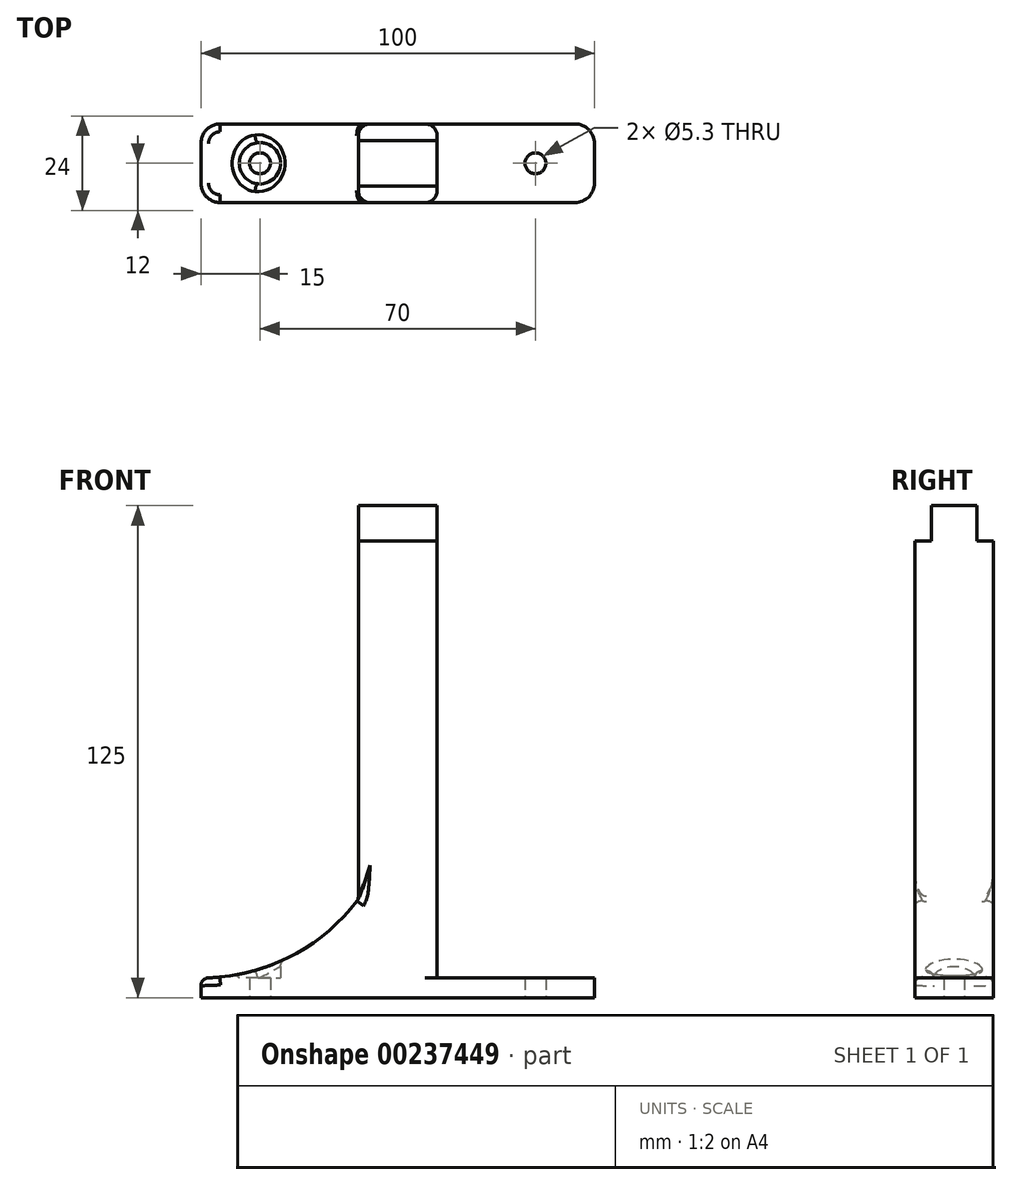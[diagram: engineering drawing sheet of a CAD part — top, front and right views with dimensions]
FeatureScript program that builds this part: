
annotation { "Feature Type Name" : "Feature", "Feature Type Description" : "" }
export const myFeature = defineFeature(function(context is Context, id is Id, definition is map)
    precondition{}
    {
        {
            var Q0;
            Q0=qCreatedBy(makeId("Front.planeOp"),FACE);
            var sketch = newSketch(context, id + "F0", { "sketchPlane" : qUnion([Q0])});
            skLineSegment(sketch, "E0.bottom", {"start": v(0, 0) * mm, "end": v(20, 0) * mm});
            skLineSegment(sketch, "E0.top", {"start": v(0, 120) * mm, "end": v(20, 120) * mm});
            skLineSegment(sketch, "E0.left", {"start": v(0, 0) * mm, "end": v(0, 120) * mm});
            skLineSegment(sketch, "E0.right", {"start": v(20, 0) * mm, "end": v(20, 120) * mm});
            skLineSegment(sketch, "E1", {"start": v(0, 20) * mm, "end": v(20, 20) * mm});
            skPoint(sketch, "E2.firstSnap0", {"position": v(10, 0) * mm});
            skLineSegment(sketch, "E2.bottom", {"start": v(60, 0) * mm, "end": v(-40, 0) * mm});
            skLineSegment(sketch, "E2.top", {"start": v(60, -5) * mm, "end": v(-40, -5) * mm});
            skLineSegment(sketch, "E2.left", {"start": v(60, 0) * mm, "end": v(60, -5) * mm});
            skLineSegment(sketch, "E2.right", {"start": v(-40, 0) * mm, "end": v(-40, -5) * mm});
            skLineSegment(sketch, "E3", {"start": v(10, 0) * mm, "end": v(10, 120) * mm, "construction": true});
            skArc(sketch, "E4", {"start": v(-40, 0) * mm, "mid": v(-17.64, 5.28) * mm, "end": v(0, 20) * mm});
            skArc(sketch, "E5.MirrorCS", {"start": v(60, 0) * mm, "mid": v(37.64, 5.28) * mm, "end": v(20, 20) * mm});
            skSolve(sketch);
        }
        {
            var Q0;
            {var subQ0=sQuery(id+"F0.wireOp",EDGE,"E0.top");Q0=makeQuery(id+"F0.imprint","IMPRINT",FACE,{"disambiguationData":[TD([[makeQuery(id+"F0.imprint","IMPRINT",EDGE,{"derivedFrom":subQ0}),-1.0]])]});}
            var Q1;
            {var subQ3=sQuery(id+"F0.wireOp",EDGE,"E1");Q1=makeQuery(id+"F0.imprint","IMPRINT",FACE,{"disambiguationData":[TD([[makeQuery(id+"F0.imprint","IMPRINT",EDGE,{"derivedFrom":subQ3}),-1.0]])]});}
            var Q2;
            {var subQ3=sQuery(id+"F0.wireOp",EDGE,"E4");Q2=makeQuery(id+"F0.imprint","IMPRINT",FACE,{"disambiguationData":[TD([[makeQuery(id+"F0.imprint","IMPRINT",EDGE,{"derivedFrom":subQ3}),-1.0]])]});}
            var Q3;
            {var subQ3=sQuery(id+"F0.wireOp",EDGE,"E5.MirrorCS");Q3=makeQuery(id+"F0.imprint","IMPRINT",FACE,{"disambiguationData":[TD([[makeQuery(id+"F0.imprint","IMPRINT",EDGE,{"derivedFrom":subQ3}),1.0]])]});}
            var Q4;
            Q4=makeQuery(id+"F0.imprint","IMPRINT",FACE,{"disambiguationData":[TD([[makeQuery(id+"F0.imprint","IMPRINT",EDGE,{"derivedFrom":sQuery(id+"F0.wireOp",EDGE,"E2.top")}),-1.0]])]});
            extrude(context, id + "F1", {"entities" : qUnion([Q0, Q1, Q2, Q3, Q4]), "depth" : 20 * mm});
        }
        {
            var Q0;
            Q0=makeQuery(id+"F1.opExtrude","SWEPT_FACE",FACE,{"disambiguationData":[OSD([sQuery(id+"F0.wireOp",EDGE,"E0.top")])]});
            var sketch = newSketch(context, id + "F2", { "sketchPlane" : qUnion([Q0])});
            skLineSegment(sketch, "E6.bottom", {"start": v(20, -15.75) * mm, "end": v(0, -15.75) * mm});
            skLineSegment(sketch, "E6.top", {"start": v(20, -4.25) * mm, "end": v(0, -4.25) * mm});
            skLineSegment(sketch, "E6.left", {"start": v(20, -15.75) * mm, "end": v(20, -4.25) * mm});
            skLineSegment(sketch, "E6.right", {"start": v(0, -15.75) * mm, "end": v(0, -4.25) * mm});
            skPoint(sketch, "E6.middle", {"position": v(10, -10) * mm});
            skSolve(sketch);
        }
        {
            var Q0;
            {var subQ0=sQuery(id+"F2.wireOp",EDGE,"E6.bottom");Q0=makeQuery(id+"F2.imprint","IMPRINT",FACE,{"disambiguationData":[TD([[makeQuery(id+"F2.imprint","IMPRINT",EDGE,{"derivedFrom":subQ0}),1.0]])]});}
            var Q1;
            {var subQ0=sQuery(id+"F2.wireOp",EDGE,"E6.top");Q1=makeQuery(id+"F2.imprint","IMPRINT",FACE,{"disambiguationData":[TD([[makeQuery(id+"F2.imprint","IMPRINT",EDGE,{"derivedFrom":subQ0}),-1.0]])]});}
            extrude(context, id + "F3", {"entities" : qUnion([Q0, Q1]), "operationType" : NewBodyOperationType.REMOVE, "oppositeDirection" : true, "depth" : 9 * mm});
        }
        {
            var Q0;
            Q0=makeQuery(id+"F1.opExtrude","SWEPT_FACE",FACE,{"disambiguationData":[OSD([sQuery(id+"F0.wireOp",EDGE,"E2.top")])]});
            var sketch = newSketch(context, id + "F4", { "sketchPlane" : qUnion([Q0])});
            skCircle(sketch, "E7", {"center": v(-25, 10) * mm, "radius": 2.65 * mm});
            skCircle(sketch, "E8", {"center": v(45, 10) * mm, "radius": 2.65 * mm});
            skLineSegment(sketch, "E9", {"start": v(-40, 10) * mm, "end": v(60, 10) * mm, "construction": true});
            skLineSegment(sketch, "E10", {"start": v(10, 0) * mm, "end": v(10, 20) * mm, "construction": true});
            skCircle(sketch, "E11", {"center": v(-25, 10) * mm, "radius": 5.25 * mm});
            skCircle(sketch, "E12", {"center": v(45, 10) * mm, "radius": 5.25 * mm});
            skSolve(sketch);
        }
        {
            var Q0;
            Q0=makeQuery(id+"F4.imprint","IMPRINT",FACE,{"disambiguationData":[TD([[makeQuery(id+"F4.imprint","IMPRINT",EDGE,{"derivedFrom":sQuery(id+"F4.wireOp",EDGE,"E7")}),1.0]])]});
            var Q1;
            Q1=makeQuery(id+"F4.imprint","IMPRINT",FACE,{"disambiguationData":[TD([[makeQuery(id+"F4.imprint","IMPRINT",EDGE,{"derivedFrom":sQuery(id+"F4.wireOp",EDGE,"E8")}),1.0]])]});
            extrude(context, id + "F5", {"entities" : qUnion([Q0, Q1]), "operationType" : NewBodyOperationType.REMOVE, "endBound" : BoundingType.THROUGH_ALL, "oppositeDirection" : true, "depth" : 25 * mm});
        }
        {
            var Q0;
            Q0=qCreatedBy(makeId("Top.planeOp"),FACE);
            var sketch = newSketch(context, id + "F6", { "sketchPlane" : qUnion([Q0])});
            skCircle(sketch, "E13.0", {"center": v(-25, -10) * mm, "radius": 5.25 * mm});
            skCircle(sketch, "E13.1", {"center": v(45, -10) * mm, "radius": 5.25 * mm});
            skSolve(sketch);
        }
        {
            var Q0;
            Q0 = qSketchRegion(id + "F6", true);
            extrude(context, id + "F7", {"entities" : qUnion([Q0]), "operationType" : NewBodyOperationType.REMOVE, "endBound" : BoundingType.THROUGH_ALL, "depth" : 25 * mm});
        }
        {
            var Q0;
            Q0=makeQuery(id+"F1.opExtrude","CAP_EDGE",EDGE,{"disambiguationData":[OSD([sQuery(id+"F0.wireOp",EDGE,"E2.left")])],"isStart":false});
            var Q1;
            Q1=makeQuery(id+"F1.opExtrude","CAP_EDGE",EDGE,{"disambiguationData":[OSD([sQuery(id+"F0.wireOp",EDGE,"E2.left")])],"isStart":true});
            var Q2;
            Q2=makeQuery(id+"F1.opExtrude","CAP_EDGE",EDGE,{"disambiguationData":[OSD([sQuery(id+"F0.wireOp",EDGE,"E2.right")])],"isStart":false});
            var Q3;
            Q3=makeQuery(id+"F1.opExtrude","CAP_EDGE",EDGE,{"disambiguationData":[OSD([sQuery(id+"F0.wireOp",EDGE,"E2.right")])],"isStart":true});
            fillet(context, id + "F8", {"entities" : qUnion([Q0, Q1, Q2, Q3]), "radius" : 5 * mm, "tangentPropagation" : true, "allowEdgeOverflow" : false});
        }
        {
            var Q0;
            Q0=makeQuery(id+"F1.opExtrude","CAP_EDGE",EDGE,{"disambiguationData":[OSD([sQuery(id+"F0.wireOp",EDGE,"E0.left")])],"isStart":true});
            var Q1;
            Q1=makeQuery(id+"F1.opExtrude","CAP_EDGE",EDGE,{"disambiguationData":[OSD([sQuery(id+"F0.wireOp",EDGE,"E0.right")])],"isStart":true});
            var Q2;
            Q2=makeQuery(id+"F1.opExtrude","CAP_EDGE",EDGE,{"disambiguationData":[OSD([sQuery(id+"F0.wireOp",EDGE,"E0.left")])],"isStart":false});
            var Q3;
            Q3=makeQuery(id+"F1.opExtrude","CAP_EDGE",EDGE,{"disambiguationData":[OSD([sQuery(id+"F0.wireOp",EDGE,"E0.right")])],"isStart":false});
            var Q4;
            {var subQ0=sQuery(id+"F0.wireOp",EDGE,"E0.top");Q4=makeQuery(id+"F3.boolean.opBoolean","COPY",EDGE,{"derivedFrom":makeQuery(id+"F3.opExtrude","CAP_EDGE",EDGE,{"disambiguationData":[OSD([subQ0]),TDD([makeQuery(id+"F2.imprint","IMPRINT",EDGE,{"derivedFrom":makeQuery(id+"F1.opExtrude","CAP_EDGE",EDGE,{"disambiguationData":[OSD([subQ0])],"isStart":false})})])],"isStart":false})});}
            var Q5;
            {var subQ0=sQuery(id+"F0.wireOp",EDGE,"E0.top");Q5=makeQuery(id+"F3.boolean.opBoolean","COPY",EDGE,{"derivedFrom":makeQuery(id+"F3.opExtrude","CAP_EDGE",EDGE,{"disambiguationData":[OSD([subQ0]),TDD([makeQuery(id+"F2.imprint","IMPRINT",EDGE,{"derivedFrom":makeQuery(id+"F1.opExtrude","CAP_EDGE",EDGE,{"disambiguationData":[OSD([subQ0])],"isStart":true})})])],"isStart":false})});}
            fillet(context, id + "F9", {"entities" : qUnion([Q0, Q1, Q2, Q3, Q4, Q5]), "radius" : 3 * mm, "tangentPropagation" : true, "allowEdgeOverflow" : false});
        }
        {
            var Q0;
            Q0=makeQuery(id+"F1.opExtrude","SWEPT_FACE",FACE,{"disambiguationData":[OSD([sQuery(id+"F0.wireOp",EDGE,"E4")])]});
            var Q1;
            Q1=makeQuery(id+"F1.opExtrude","SWEPT_FACE",FACE,{"disambiguationData":[OSD([sQuery(id+"F0.wireOp",EDGE,"E5.MirrorCS")])]});
            fillet(context, id + "F10", {"entities" : qUnion([Q0, Q1]), "radius" : 2 * mm, "tangentPropagation" : true, "allowEdgeOverflow" : false});
        }
    });
